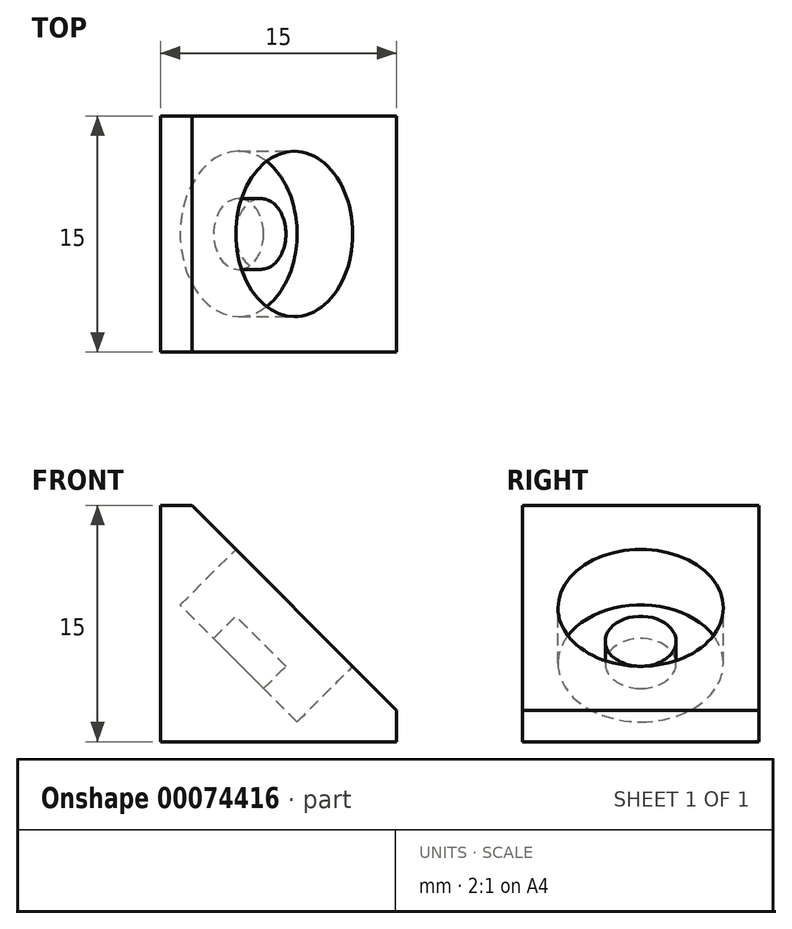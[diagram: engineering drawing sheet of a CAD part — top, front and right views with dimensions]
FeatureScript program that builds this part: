
annotation { "Feature Type Name" : "Feature", "Feature Type Description" : "" }
export const myFeature = defineFeature(function(context is Context, id is Id, definition is map)
    precondition{}
    {
        {
            var Q0;
            Q0=qCreatedBy(makeId("Top.planeOp"),FACE);
            var sketch = newSketch(context, id + "F0", { "sketchPlane" : qUnion([Q0])});
            skLineSegment(sketch, "E0.bottom", {"start": v(0, 0) * mm, "end": v(15, 0) * mm});
            skLineSegment(sketch, "E0.top", {"start": v(0, -15) * mm, "end": v(15, -15) * mm});
            skLineSegment(sketch, "E0.left", {"start": v(0, 0) * mm, "end": v(0, -15) * mm});
            skLineSegment(sketch, "E0.right", {"start": v(15, 0) * mm, "end": v(15, -15) * mm});
            skSolve(sketch);
        }
        {
            var Q0;
            Q0=makeQuery(id+"F0.imprint","IMPRINT",FACE,{"disambiguationData":[TD([[makeQuery(id+"F0.imprint","IMPRINT",EDGE,{"derivedFrom":sQuery(id+"F0.wireOp",EDGE,"E0.bottom")}),-1.0]])]});
            extrude(context, id + "F1", {"entities" : qUnion([Q0]), "depth" : 15 * mm});
        }
        {
            var Q0;
            Q0=makeQuery(id+"F1.opExtrude","CAP_EDGE",EDGE,{"disambiguationData":[OSD([sQuery(id+"F0.wireOp",EDGE,"E0.right")])],"isStart":false});
            chamfer(context, id + "F2", {"entities" : qUnion([Q0]), "width" : 13 * mm, "tangentPropagation" : true});
        }
        {
            var Q0;
            Q0=makeQuery(id+"F2.opChamfer","BLEND_FACE",FACE,{"disambiguationData":[OSD([sQuery(id+"F0.wireOp",EDGE,"E0.right")])]});
            var sketch = newSketch(context, id + "F3", { "sketchPlane" : qUnion([Q0])});
            skLineSegment(sketch, "E1", {"start": v(-15, 0) * mm, "end": v(0, 0) * mm, "construction": true});
            skCircle(sketch, "E2", {"center": v(-7.5, 0) * mm, "radius": 5.25 * mm});
            skCircle(sketch, "E3", {"center": v(-7.5, 0) * mm, "radius": 2.25 * mm});
            skSolve(sketch);
        }
        {
            var Q0;
            Q0=makeQuery(id+"F3.imprint","IMPRINT",FACE,{"disambiguationData":[TD([[makeQuery(id+"F3.imprint","IMPRINT",EDGE,{"derivedFrom":sQuery(id+"F3.wireOp",EDGE,"E2")}),1.0]])]});
            extrude(context, id + "F4", {"entities" : qUnion([Q0]), "operationType" : NewBodyOperationType.REMOVE, "oppositeDirection" : true, "depth" : 5 * mm});
        }
        {
            var Q0;
            Q0=makeQuery(id+"F4.boolean.opBoolean","SPLIT",FACE,{"disambiguationData":[TD([makeQuery(id+"F4.opExtrude","SWEPT_FACE",FACE,{"disambiguationData":[OSD([sQuery(id+"F3.wireOp",EDGE,"E3")])]})])],"derivedFrom":makeQuery(id+"F2.opChamfer","BLEND_FACE",FACE,{"disambiguationData":[OSD([sQuery(id+"F0.wireOp",EDGE,"E0.right")])]})});
            extrude(context, id + "F5", {"entities" : qUnion([Q0]), "operationType" : NewBodyOperationType.REMOVE, "oppositeDirection" : true, "depth" : 3 * mm});
        }
    });
